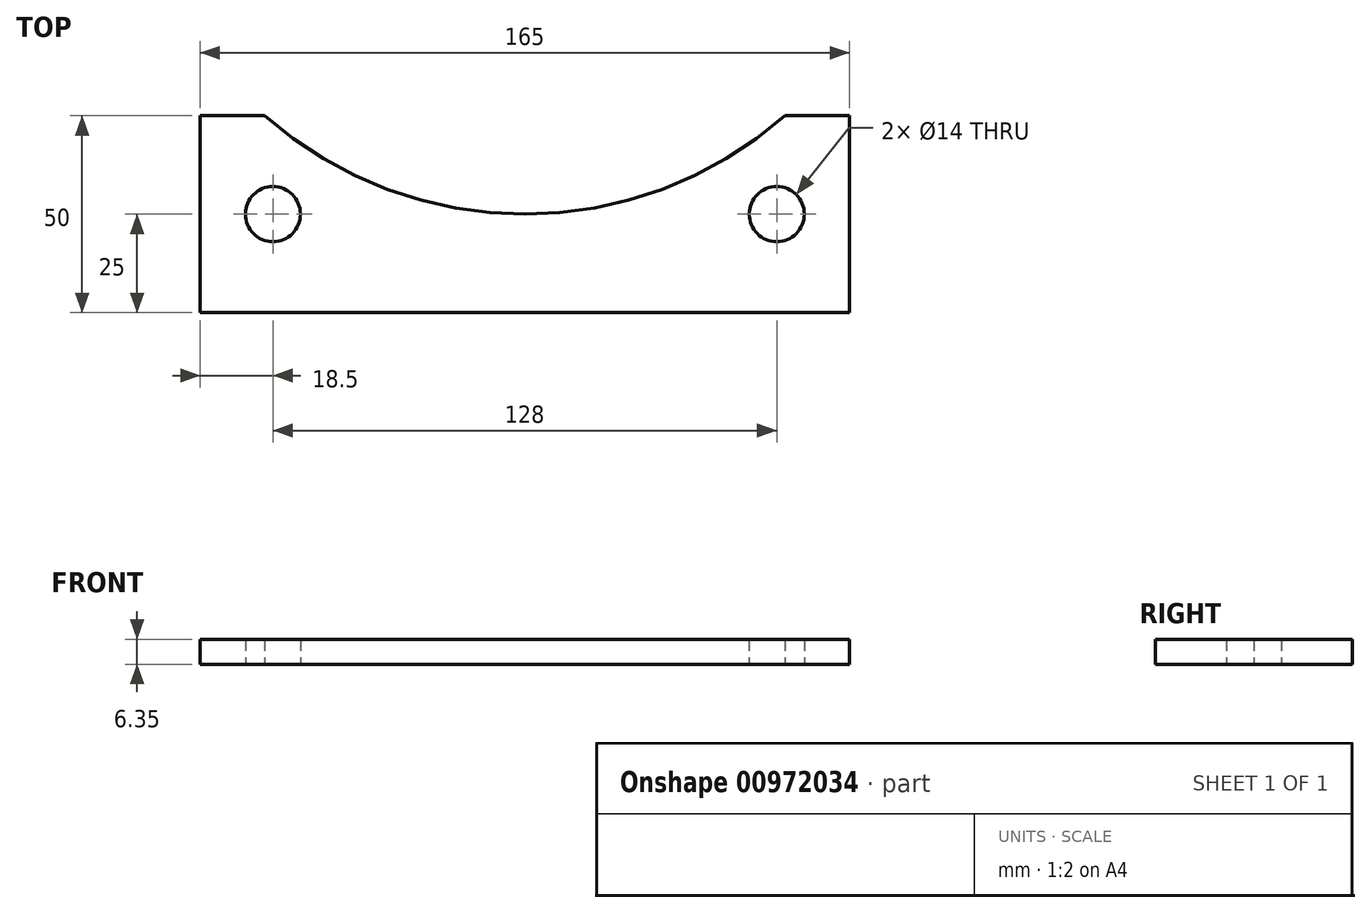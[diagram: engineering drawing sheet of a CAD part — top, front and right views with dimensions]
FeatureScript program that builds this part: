
annotation { "Feature Type Name" : "Feature", "Feature Type Description" : "" }
export const myFeature = defineFeature(function(context is Context, id is Id, definition is map)
    precondition{}
    {
        {
            var Q0;
            Q0=qCreatedBy(makeId("Top.planeOp"),FACE);
            var sketch = newSketch(context, id + "F0", { "sketchPlane" : qUnion([Q0])});
            skLineSegment(sketch, "E0", {"start": v(0, 75) * mm, "end": v(0, -25) * mm, "construction": true});
            skLineSegment(sketch, "E1.bottom", {"start": v(-82.5, 0) * mm, "end": v(-66.14, 0) * mm});
            skLineSegment(sketch, "E1.top", {"start": v(-82.5, -50) * mm, "end": v(82.5, -50) * mm});
            skLineSegment(sketch, "E1.left", {"start": v(-82.5, 0) * mm, "end": v(-82.5, -50) * mm});
            skLineSegment(sketch, "E1.right", {"start": v(82.5, 0) * mm, "end": v(82.5, -50) * mm});
            skLineSegment(sketch, "E2", {"start": v(-82.5, -25) * mm, "end": v(82.5, -25) * mm, "construction": true});
            skArc(sketch, "E3", {"start": v(-66.14, 0) * mm, "mid": v(0, -25) * mm, "end": v(66.14, 0) * mm});
            skLineSegment(sketch, "E4.trimOffspring", {"start": v(66.14, 0) * mm, "end": v(82.5, 0) * mm});
            skLineSegment(sketch, "E5.0", {"start": v(-64, 75) * mm, "end": v(-64, -25) * mm, "construction": true});
            skPoint(sketch, "E6", {"position": v(64, -25) * mm});
            skPoint(sketch, "E7", {"position": v(-64, -25) * mm});
            skSolve(sketch);
        }
        {
            var Q0;
            Q0 = qSketchRegion(id + "F0", true);
            extrude(context, id + "F1", {"entities" : qUnion([Q0]), "depth" : 6.35 * mm, "offsetDistance" : 25 * mm});
        }
        {
            var Q0;
            Q0=sQuery(id+"F0.wireOp",VERTEX,"E7");
            var Q1;
            Q1=sQuery(id+"F0.wireOp",VERTEX,"E6");
            var Q2;
            Q2=makeQuery(id+"F1.opExtrude","SWEPT_BODY",BODY,{"disambiguationData":[OSD([sQuery(id+"F0.wireOp",EDGE,"E1.bottom"),sQuery(id+"F0.wireOp",EDGE,"E1.top"),sQuery(id+"F0.wireOp",EDGE,"E1.left"),sQuery(id+"F0.wireOp",EDGE,"E1.right"),sQuery(id+"F0.wireOp",EDGE,"E3"),sQuery(id+"F0.wireOp",EDGE,"E4.trimOffspring")])]});
            hole(context, id + "F2", {"style" : HoleStyle.SIMPLE, "endStyle" : HoleEndStyle.THROUGH, "oppositeDirection" : true, "standardTappedOrClearance" : lookupTablePath({ "standard" : "ISO", "size" : "14", "type" : "Drilled" }), "standardBlindInLast" : lookupTablePath({ "standard" : "ISO", "size" : "14", "type" : "Drilled" }), "holeDiameter" : 14 * mm, "majorDiameter" : 4 * mm, "isTappedThrough" : true, "tappedDepth" : 12 * mm, "tapClearance" : 3, "locations" : qUnion([Q0, Q1]), "scope" : qUnion([Q2])});
        }
    });
